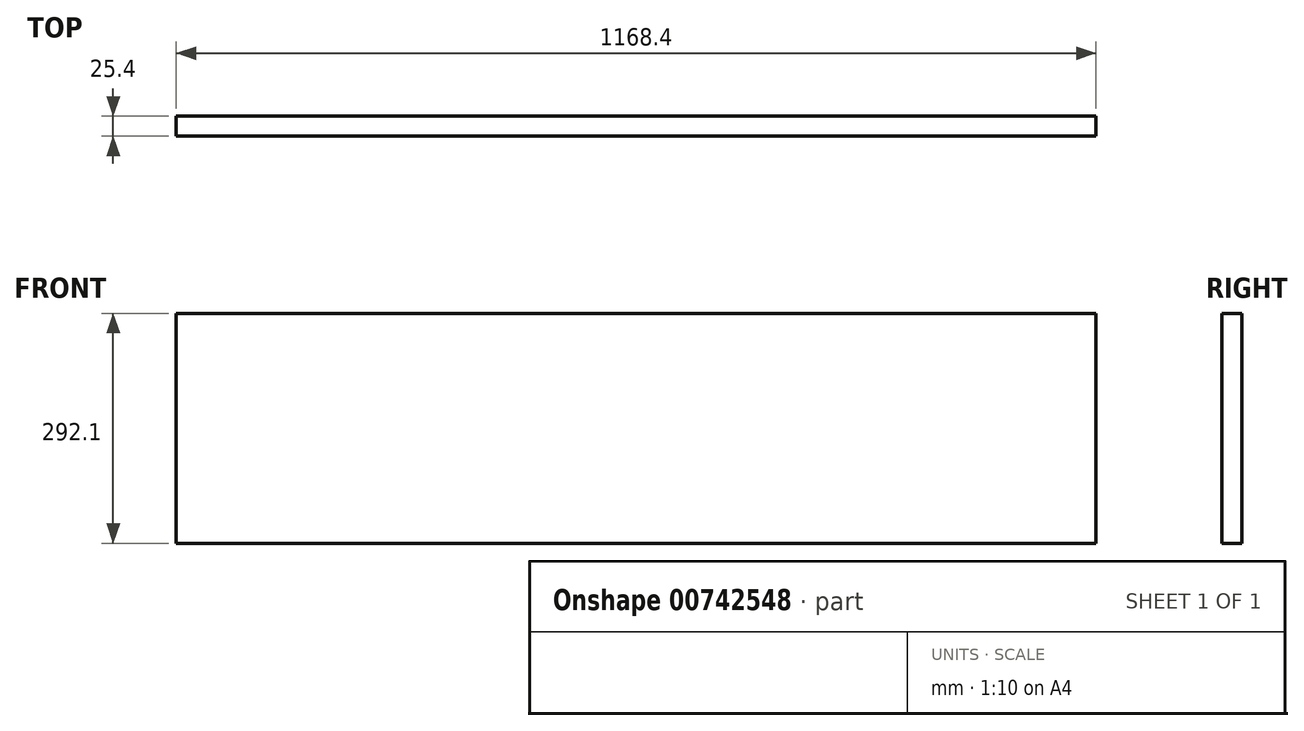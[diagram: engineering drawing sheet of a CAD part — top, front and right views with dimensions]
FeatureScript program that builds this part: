
annotation { "Feature Type Name" : "Feature", "Feature Type Description" : "" }
export const myFeature = defineFeature(function(context is Context, id is Id, definition is map)
    precondition{}
    {
        {
            var Q0;
            Q0=qCreatedBy(makeId("Front.planeOp"),FACE);
            var sketch = newSketch(context, id + "F0", { "sketchPlane" : qUnion([Q0])});
            skLineSegment(sketch, "E0.bottom", {"start": v(584.2, 146.05) * mm, "end": v(-584.2, 146.05) * mm});
            skLineSegment(sketch, "E0.top", {"start": v(584.2, -146.05) * mm, "end": v(-584.2, -146.05) * mm});
            skLineSegment(sketch, "E0.left", {"start": v(584.2, 146.05) * mm, "end": v(584.2, -146.05) * mm});
            skLineSegment(sketch, "E0.right", {"start": v(-584.2, 146.05) * mm, "end": v(-584.2, -146.05) * mm});
            skPoint(sketch, "E0.middle", {"position": v(0, 0) * mm});
            skSolve(sketch);
        }
        {
            var Q0;
            Q0 = qSketchRegion(id + "F0", true);
            extrude(context, id + "F1", {"entities" : qUnion([Q0]), "depth" : 25.4 * mm, "offsetDistance" : 25.4 * mm});
        }
    });
